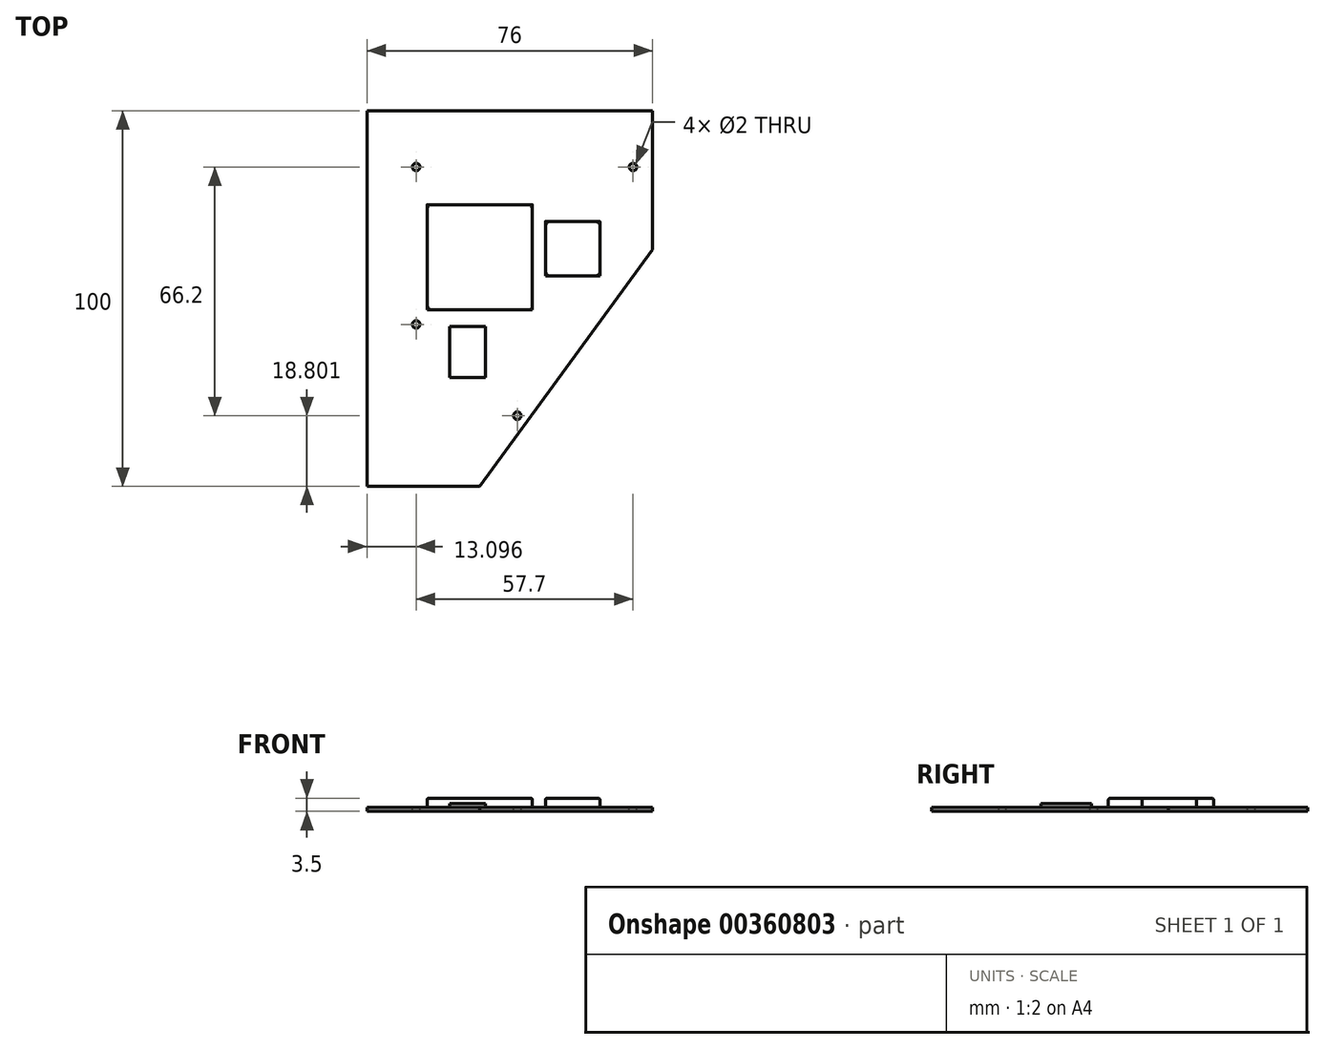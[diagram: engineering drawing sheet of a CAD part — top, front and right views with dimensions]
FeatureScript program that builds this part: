
annotation { "Feature Type Name" : "Feature", "Feature Type Description" : "" }
export const myFeature = defineFeature(function(context is Context, id is Id, definition is map)
    precondition{}
    {
        {
            var Q0;
            Q0=qCreatedBy(makeId("Top.planeOp"),FACE);
            var sketch = newSketch(context, id + "F0", { "sketchPlane" : qUnion([Q0])});
            skLineSegment(sketch, "E0.bottom", {"start": v(-41.76, -58.97) * mm, "end": v(-11.76, -58.97) * mm});
            skLineSegment(sketch, "E0.top", {"start": v(-41.76, 41.03) * mm, "end": v(34.24, 41.03) * mm});
            skLineSegment(sketch, "E0.left", {"start": v(-41.76, -58.97) * mm, "end": v(-41.76, 41.03) * mm});
            skLineSegment(sketch, "E0.right", {"start": v(34.24, 4.03) * mm, "end": v(34.24, 41.03) * mm});
            skLineSegment(sketch, "E1", {"start": v(-11.76, -58.97) * mm, "end": v(34.24, 4.03) * mm});
            skSolve(sketch);
        }
        {
            var Q0;
            Q0=makeQuery(id+"F0.imprint","IMPRINT",FACE,{"disambiguationData":[TD([[makeQuery(id+"F0.imprint","IMPRINT",EDGE,{"derivedFrom":sQuery(id+"F0.wireOp",EDGE,"E0.bottom")}),1.0]])]});
            extrude(context, id + "F1", {"entities" : qUnion([Q0]), "depth" : 1 * mm});
        }
        {
            var Q0;
            Q0=makeQuery(id+"F1.opExtrude","CAP_FACE",FACE,{"disambiguationData":[OSD([sQuery(id+"F0.wireOp",EDGE,"E0.bottom"),sQuery(id+"F0.wireOp",EDGE,"E0.top"),sQuery(id+"F0.wireOp",EDGE,"E0.left"),sQuery(id+"F0.wireOp",EDGE,"E0.right"),sQuery(id+"F0.wireOp",EDGE,"E1")])],"isStart":false});
            var sketch = newSketch(context, id + "F2", { "sketchPlane" : qUnion([Q0])});
            skCircle(sketch, "E2", {"center": v(29.04, 26.03) * mm, "radius": 1 * mm});
            skCircle(sketch, "E3", {"center": v(-28.66, 26.03) * mm, "radius": 1 * mm});
            skCircle(sketch, "E4", {"center": v(-28.66, -15.87) * mm, "radius": 1 * mm});
            skCircle(sketch, "E5", {"center": v(-1.76, -40.17) * mm, "radius": 1 * mm});
            skSolve(sketch);
        }
        {
            var Q0;
            Q0=makeQuery(id+"F2.imprint","IMPRINT",FACE,{"disambiguationData":[TD([[makeQuery(id+"F2.imprint","IMPRINT",EDGE,{"derivedFrom":sQuery(id+"F2.wireOp",EDGE,"E3")}),1.0]])]});
            var Q1;
            Q1=makeQuery(id+"F2.imprint","IMPRINT",FACE,{"disambiguationData":[TD([[makeQuery(id+"F2.imprint","IMPRINT",EDGE,{"derivedFrom":sQuery(id+"F2.wireOp",EDGE,"E4")}),1.0]])]});
            var Q2;
            Q2=makeQuery(id+"F2.imprint","IMPRINT",FACE,{"disambiguationData":[TD([[makeQuery(id+"F2.imprint","IMPRINT",EDGE,{"derivedFrom":sQuery(id+"F2.wireOp",EDGE,"E2")}),1.0]])]});
            var Q3;
            Q3=makeQuery(id+"F2.imprint","IMPRINT",FACE,{"disambiguationData":[TD([[makeQuery(id+"F2.imprint","IMPRINT",EDGE,{"derivedFrom":sQuery(id+"F2.wireOp",EDGE,"E5")}),1.0]])]});
            extrude(context, id + "F3", {"entities" : qUnion([Q0, Q1, Q2, Q3]), "operationType" : NewBodyOperationType.REMOVE, "oppositeDirection" : true, "depth" : 2 * mm});
        }
        {
            var Q0;
            Q0=makeQuery(id+"F1.opExtrude","CAP_FACE",FACE,{"disambiguationData":[OSD([sQuery(id+"F0.wireOp",EDGE,"E0.bottom"),sQuery(id+"F0.wireOp",EDGE,"E0.top"),sQuery(id+"F0.wireOp",EDGE,"E0.left"),sQuery(id+"F0.wireOp",EDGE,"E0.right"),sQuery(id+"F0.wireOp",EDGE,"E1")])],"isStart":false});
            var sketch = newSketch(context, id + "F4", { "sketchPlane" : qUnion([Q0])});
            skLineSegment(sketch, "E6.bottom", {"start": v(-25.76, -11.97) * mm, "end": v(2.24, -11.97) * mm});
            skLineSegment(sketch, "E6.top", {"start": v(-25.76, 16.03) * mm, "end": v(2.24, 16.03) * mm});
            skLineSegment(sketch, "E6.left", {"start": v(-25.76, -11.97) * mm, "end": v(-25.76, 16.03) * mm});
            skLineSegment(sketch, "E6.right", {"start": v(2.24, -11.97) * mm, "end": v(2.24, 16.03) * mm});
            skLineSegment(sketch, "E7.bottom", {"start": v(5.74, -2.97) * mm, "end": v(20.24, -2.97) * mm});
            skLineSegment(sketch, "E7.top", {"start": v(5.74, 11.53) * mm, "end": v(20.24, 11.53) * mm});
            skLineSegment(sketch, "E7.left", {"start": v(5.74, -2.97) * mm, "end": v(5.74, 11.53) * mm});
            skLineSegment(sketch, "E7.right", {"start": v(20.24, -2.97) * mm, "end": v(20.24, 11.53) * mm});
            skSolve(sketch);
        }
        {
            var Q0;
            Q0=makeQuery(id+"F4.imprint","IMPRINT",FACE,{"disambiguationData":[TD([[makeQuery(id+"F4.imprint","IMPRINT",EDGE,{"derivedFrom":sQuery(id+"F4.wireOp",EDGE,"E6.bottom")}),1.0]])]});
            var Q1;
            Q1=makeQuery(id+"F4.imprint","IMPRINT",FACE,{"disambiguationData":[TD([[makeQuery(id+"F4.imprint","IMPRINT",EDGE,{"derivedFrom":sQuery(id+"F4.wireOp",EDGE,"E7.bottom")}),1.0]])]});
            extrude(context, id + "F5", {"entities" : qUnion([Q0, Q1]), "operationType" : NewBodyOperationType.ADD, "depth" : 2.5 * mm});
        }
        {
            var Q0;
            Q0=makeQuery(id+"F5.opExtrude","CAP_EDGE",EDGE,{"disambiguationData":[OSD([sQuery(id+"F4.wireOp",EDGE,"E6.bottom")])],"isStart":false});
            var Q1;
            Q1=makeQuery(id+"F5.opExtrude","CAP_EDGE",EDGE,{"disambiguationData":[OSD([sQuery(id+"F4.wireOp",EDGE,"E6.left")])],"isStart":false});
            var Q2;
            Q2=makeQuery(id+"F5.opExtrude","CAP_EDGE",EDGE,{"disambiguationData":[OSD([sQuery(id+"F4.wireOp",EDGE,"E6.top")])],"isStart":false});
            var Q3;
            Q3=makeQuery(id+"F5.opExtrude","CAP_EDGE",EDGE,{"disambiguationData":[OSD([sQuery(id+"F4.wireOp",EDGE,"E6.right")])],"isStart":false});
            var Q4;
            Q4=makeQuery(id+"F5.opExtrude","CAP_EDGE",EDGE,{"disambiguationData":[OSD([sQuery(id+"F4.wireOp",EDGE,"E7.top")])],"isStart":false});
            var Q5;
            Q5=makeQuery(id+"F5.opExtrude","CAP_EDGE",EDGE,{"disambiguationData":[OSD([sQuery(id+"F4.wireOp",EDGE,"E7.left")])],"isStart":false});
            var Q6;
            Q6=makeQuery(id+"F5.opExtrude","CAP_EDGE",EDGE,{"disambiguationData":[OSD([sQuery(id+"F4.wireOp",EDGE,"E7.bottom")])],"isStart":false});
            var Q7;
            Q7=makeQuery(id+"F5.opExtrude","CAP_EDGE",EDGE,{"disambiguationData":[OSD([sQuery(id+"F4.wireOp",EDGE,"E7.right")])],"isStart":false});
            fillet(context, id + "F6", {"entities" : qUnion([Q0, Q1, Q2, Q3, Q4, Q5, Q6, Q7]), "radius" : .5 * mm, "tangentPropagation" : true, "allowEdgeOverflow" : false});
        }
        {
            var Q0;
            Q0=makeQuery(id+"F1.opExtrude","CAP_FACE",FACE,{"disambiguationData":[OSD([sQuery(id+"F0.wireOp",EDGE,"E0.bottom"),sQuery(id+"F0.wireOp",EDGE,"E0.top"),sQuery(id+"F0.wireOp",EDGE,"E0.left"),sQuery(id+"F0.wireOp",EDGE,"E0.right"),sQuery(id+"F0.wireOp",EDGE,"E1")])],"isStart":false});
            var sketch = newSketch(context, id + "F7", { "sketchPlane" : qUnion([Q0])});
            skLineSegment(sketch, "E8.bottom", {"start": v(-19.76, -29.97) * mm, "end": v(-10.26, -29.97) * mm});
            skLineSegment(sketch, "E8.top", {"start": v(-19.76, -16.47) * mm, "end": v(-10.26, -16.47) * mm});
            skLineSegment(sketch, "E8.left", {"start": v(-19.76, -29.97) * mm, "end": v(-19.76, -16.47) * mm});
            skLineSegment(sketch, "E8.right", {"start": v(-10.26, -29.97) * mm, "end": v(-10.26, -16.47) * mm});
            skSolve(sketch);
        }
        {
            var Q0;
            Q0=makeQuery(id+"F7.imprint","IMPRINT",FACE,{"disambiguationData":[TD([[makeQuery(id+"F7.imprint","IMPRINT",EDGE,{"derivedFrom":sQuery(id+"F7.wireOp",EDGE,"E8.bottom")}),1.0]])]});
            extrude(context, id + "F8", {"entities" : qUnion([Q0]), "operationType" : NewBodyOperationType.ADD, "depth" : 1 * mm});
        }
    });
